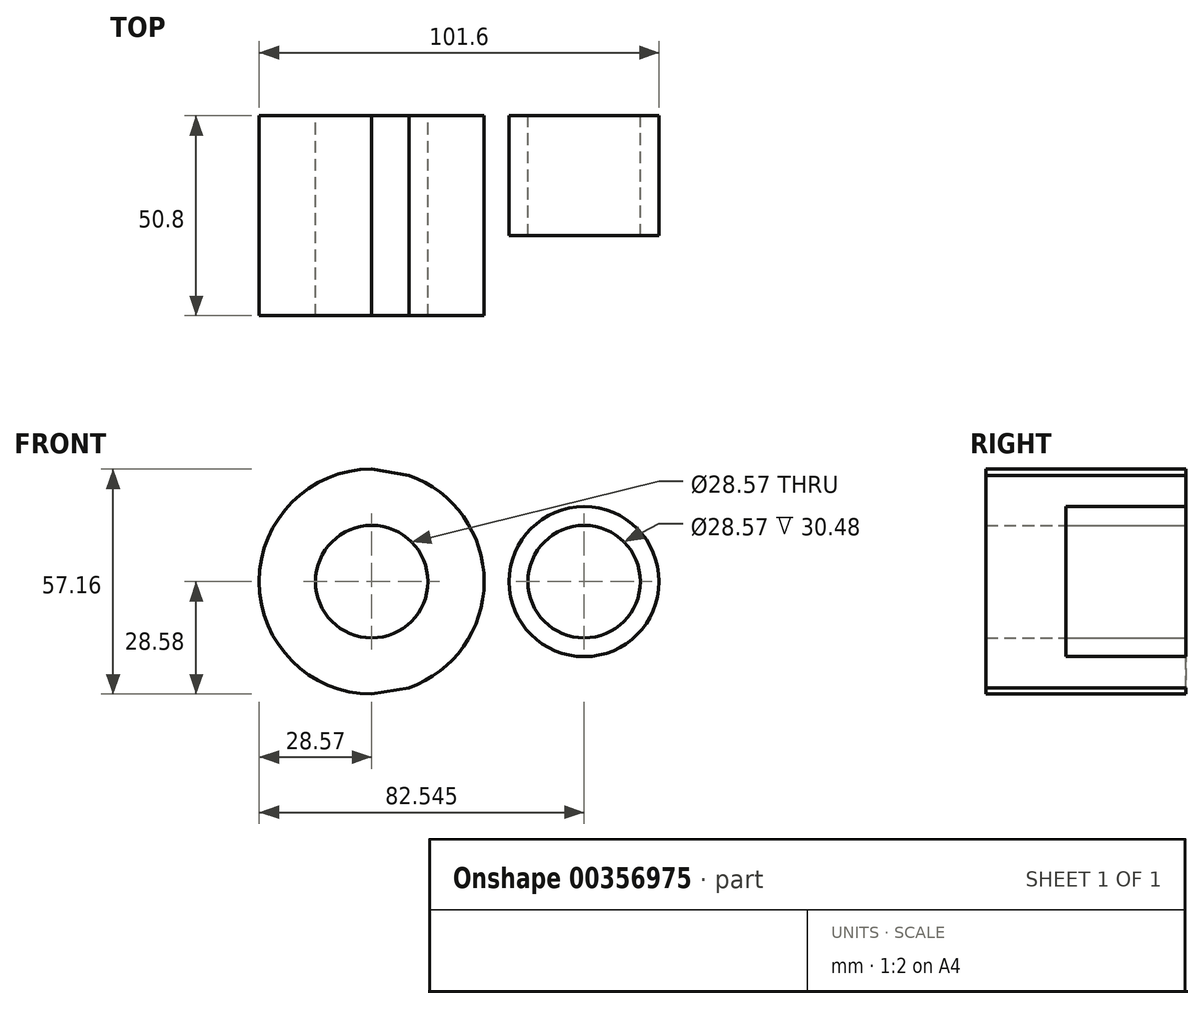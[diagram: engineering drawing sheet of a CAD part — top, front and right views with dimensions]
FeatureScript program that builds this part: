
annotation { "Feature Type Name" : "Feature", "Feature Type Description" : "" }
export const myFeature = defineFeature(function(context is Context, id is Id, definition is map)
    precondition{}
    {
        {
            var Q0;
            Q0=qCreatedBy(makeId("Front.planeOp"),FACE);
            var sketch = newSketch(context, id + "F0", { "sketchPlane" : qUnion([Q0])});
            skCircle(sketch, "E0", {"center": v(0, 0) * mm, "radius": 28.58 * mm});
            skCircle(sketch, "E1", {"center": v(53.98, 0) * mm, "radius": 19.05 * mm});
            skLineSegment(sketch, "E2", {"start": v(0, 28.57) * mm, "end": v(57.2, 18.78) * mm});
            skLineSegment(sketch, "E3", {"start": v(0, -28.57) * mm, "end": v(57.2, -18.78) * mm});
            skCircle(sketch, "E4", {"center": v(0, 0) * mm, "radius": 14.29 * mm});
            skCircle(sketch, "E5", {"center": v(53.98, 0) * mm, "radius": 14.29 * mm});
            skLineSegment(sketch, "E6.bottom", {"start": v(-19.05, 4.76) * mm, "end": v(19.05, 4.76) * mm});
            skLineSegment(sketch, "E6.top", {"start": v(-19.05, -4.76) * mm, "end": v(19.05, -4.76) * mm});
            skLineSegment(sketch, "E6.left", {"start": v(-19.05, 4.76) * mm, "end": v(-19.05, -4.76) * mm});
            skLineSegment(sketch, "E6.right", {"start": v(19.05, 4.76) * mm, "end": v(19.05, -4.76) * mm});
            skSolve(sketch);
        }
        {
            var Q0;
            {var subQ4=sQuery(id+"F0.wireOp",EDGE,"E6.left");Q0=makeQuery(id+"F0.imprint","IMPRINT",FACE,{"disambiguationData":[TD([[makeQuery(id+"F0.imprint","IMPRINT",EDGE,{"derivedFrom":subQ4}),-1.0]])]});}
            var Q1;
            {var subQ0=sQuery(id+"F0.wireOp",EDGE,"E2");var subQ1=sQuery(id+"F0.wireOp",EDGE,"E0");var subQ2=makeQuery(id+"F0.imprint","INTERSECT",VERTEX,{"disambiguationData":[OD(1.0)],"derivedFrom":[subQ1,subQ0]});Q1=makeQuery(id+"F0.imprint","IMPRINT",FACE,{"disambiguationData":[TD([[makeQuery(id+"F0.imprint","IMPRINT",EDGE,{"disambiguationData":[TD([[subQ2,1.0]])],"derivedFrom":subQ1}),-1.0]])]});}
            var Q2;
            Q2=makeQuery(id+"F0.imprint","IMPRINT",FACE,{"disambiguationData":[TD([[makeQuery(id+"F0.imprint","IMPRINT",EDGE,{"derivedFrom":sQuery(id+"F0.wireOp",EDGE,"E5")}),-1.0]])]});
            extrude(context, id + "F1", {"entities" : qUnion([Q0, Q1, Q2]), "depth" : 30.48 * mm});
        }
        {
            var Q0;
            {var subQ4=sQuery(id+"F0.wireOp",EDGE,"E6.left");Q0=makeQuery(id+"F0.imprint","IMPRINT",FACE,{"disambiguationData":[TD([[makeQuery(id+"F0.imprint","IMPRINT",EDGE,{"derivedFrom":subQ4}),-1.0]])]});}
            var Q1;
            {var subQ5=sQuery(id+"F0.wireOp",EDGE,"E6.left");Q1=makeQuery(id+"F0.imprint","IMPRINT",FACE,{"disambiguationData":[TD([[makeQuery(id+"F0.imprint","IMPRINT",EDGE,{"derivedFrom":subQ5}),1.0]])]});}
            var Q2;
            {var subQ5=sQuery(id+"F0.wireOp",EDGE,"E6.right");Q2=makeQuery(id+"F0.imprint","IMPRINT",FACE,{"disambiguationData":[TD([[makeQuery(id+"F0.imprint","IMPRINT",EDGE,{"derivedFrom":subQ5}),-1.0]])]});}
            extrude(context, id + "F2", {"entities" : qUnion([Q0, Q1, Q2]), "operationType" : NewBodyOperationType.ADD, "depth" : 50.8 * mm});
        }
    });
